# Revit family: Faucet-Deck_Mount-Bath-KOHLER-Cuff-K-98300D
name_source: partatom
category: Plumbing Fixtures
units: mm (PartAtom-declared; Revit-internal decimal feet)

## family parameters
Cut with Voids When Loaded = No
Host = Face
OmniClass Number = 23.31.11.00
OmniClass Title = Faucets
Part Type = Normal
Room Calculation Point = No
Round Connector Dimension = Use Diameter
Shared = No

## types (1)
- CP-Polished Chrome
    ADA Compliant = No
    Assembly Code = D2010
    CW Connection = Yes
    Cold Water Inlet = Cold Water Inlet
    Date Modified = 03/03/2023
    Default Elevation = 36"
    Description = Deck Mount Bath and Shower TH Mixer, CH
    Drain Included = No
    Faucet Hole Spacing = 0"
    Finish = Kohler-Metal-CP-Polished_Chrome
    Flow Rate = 0 GPM
    HW Connection = Yes
    Handle Clearance = 1 3/8"
    Height = 4 1/8"
    Hot Water Inlet = Hot Water Inlet
    Length = 7 3/8"
    Manufacturer = Kohler Co.
    Master Format 2014 = 22 41 39
    Master Format 2014 Name = Residential Faucets, Supplies, and Trim
    Material = Premium Metal Construction
    Model = K-98300D-CP
    Pressure = 0.00 psi
    Product Name = Cuff
    Spout Reach = 7 3/8"
    Tempered Water Outlet = Tempered Water Outlet
    Type = 1
    URL = https://me.kohler.com
    Vent Connection = No
    Waste Connection = No
    Waste Water Outlet = Waste Water Outlet
    WaterSense Certified = No
    Width = 5 15/16"

## geometry (parser evidence)
native form markers: Sweep x6
no freeform markers — native parametric forms only
